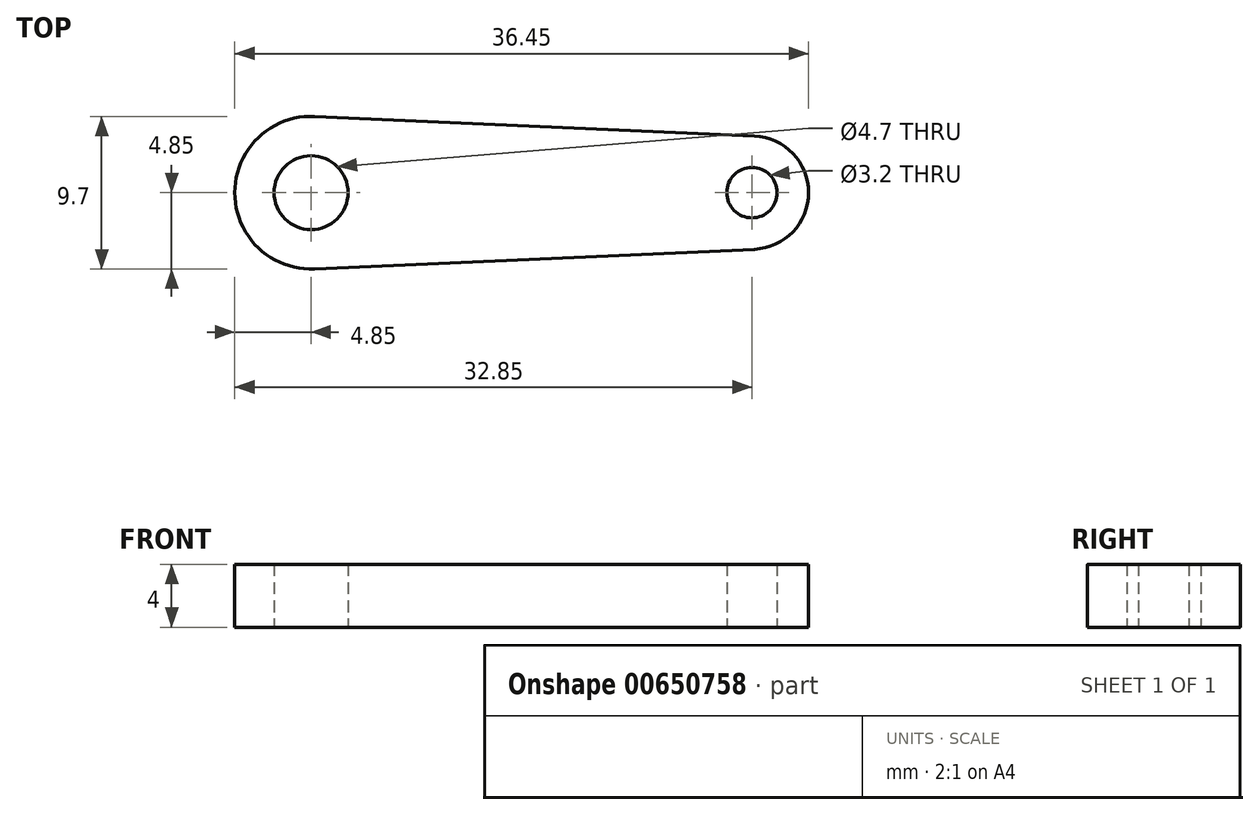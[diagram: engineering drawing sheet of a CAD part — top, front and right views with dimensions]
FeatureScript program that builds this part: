
annotation { "Feature Type Name" : "Feature", "Feature Type Description" : "" }
export const myFeature = defineFeature(function(context is Context, id is Id, definition is map)
    precondition{}
    {
        {
            var Q0;
            Q0=qCreatedBy(makeId("Top.planeOp"),FACE);
            var sketch = newSketch(context, id + "F0", { "sketchPlane" : qUnion([Q0])});
            skCircle(sketch, "E0", {"center": v(0, 0) * mm, "radius": 2.35 * mm});
            skCircle(sketch, "E1", {"center": v(0, 0) * mm, "radius": 4.85 * mm});
            skCircle(sketch, "E2", {"center": v(28, 0) * mm, "radius": 1.6 * mm});
            skCircle(sketch, "E3", {"center": v(28, 0) * mm, "radius": 3.6 * mm});
            skLineSegment(sketch, "E4", {"start": v(0.22, -4.85) * mm, "end": v(28.16, -3.6) * mm});
            skLineSegment(sketch, "E5", {"start": v(0.22, 4.85) * mm, "end": v(28.16, 3.6) * mm});
            skSolve(sketch);
        }
        {
            var Q0;
            Q0=makeQuery(id+"F0.imprint","IMPRINT",FACE,{"disambiguationData":[TD([[makeQuery(id+"F0.imprint","IMPRINT",EDGE,{"derivedFrom":sQuery(id+"F0.wireOp",EDGE,"E0")}),-1.0]])]});
            var Q1;
            {var subQ0=sQuery(id+"F0.wireOp",EDGE,"E4");Q1=makeQuery(id+"F0.imprint","IMPRINT",FACE,{"disambiguationData":[TD([[makeQuery(id+"F0.imprint","IMPRINT",EDGE,{"derivedFrom":subQ0}),1.0]])]});}
            var Q2;
            Q2=makeQuery(id+"F0.imprint","IMPRINT",FACE,{"disambiguationData":[TD([[makeQuery(id+"F0.imprint","IMPRINT",EDGE,{"derivedFrom":sQuery(id+"F0.wireOp",EDGE,"E2")}),-1.0]])]});
            extrude(context, id + "F1", {"entities" : qUnion([Q0, Q1, Q2]), "depth" : 4 * mm, "offsetDistance" : 25 * mm});
        }
    });
